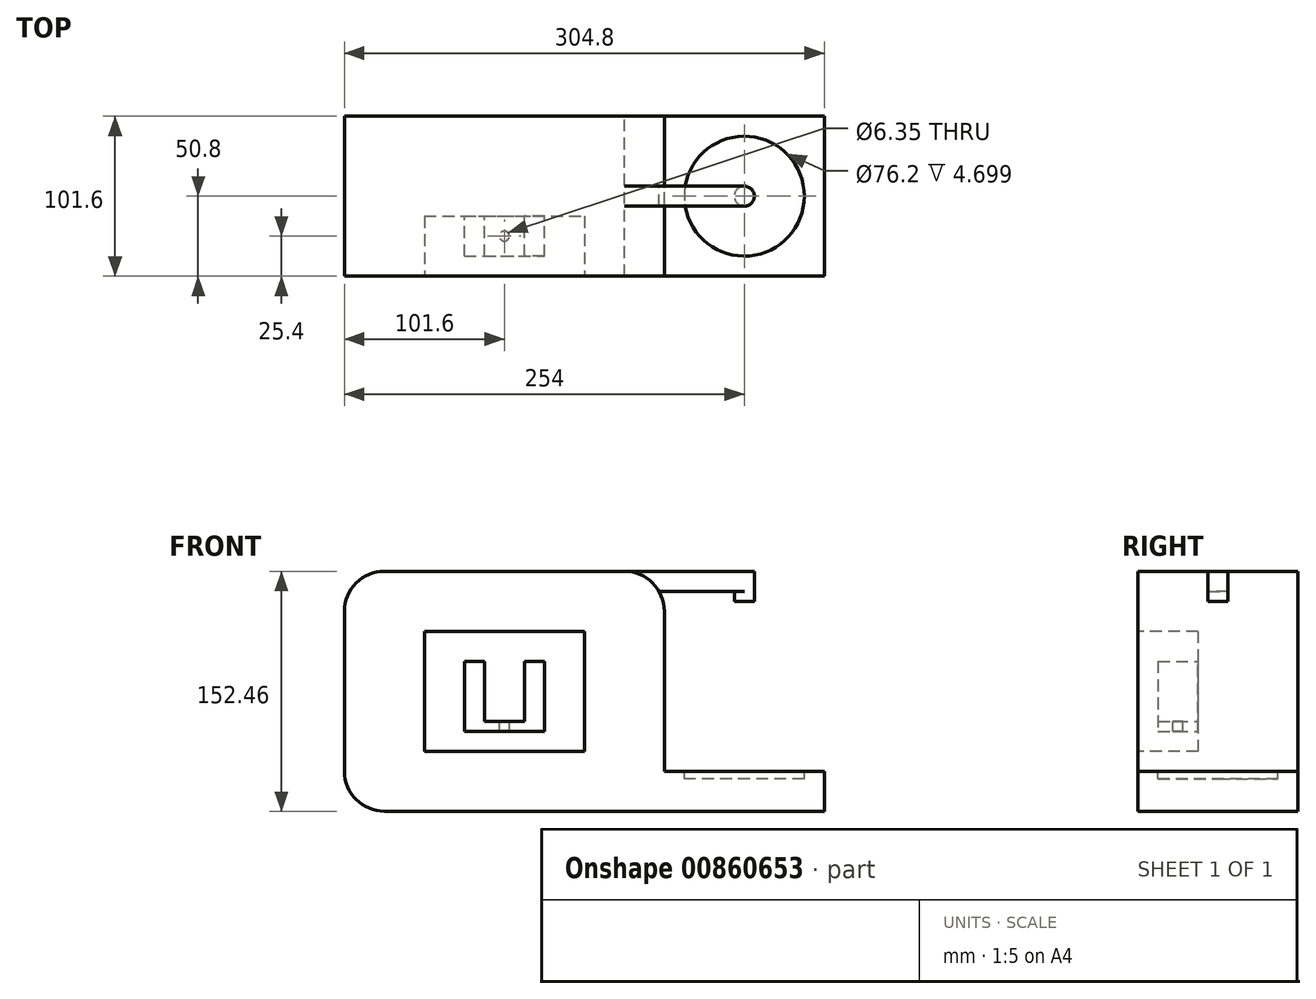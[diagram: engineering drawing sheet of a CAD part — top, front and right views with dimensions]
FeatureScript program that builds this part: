
annotation { "Feature Type Name" : "Feature", "Feature Type Description" : "" }
export const myFeature = defineFeature(function(context is Context, id is Id, definition is map)
    precondition{}
    {
        {
            var Q0;
            Q0=qCreatedBy(makeId("Front.planeOp"),FACE);
            var sketch = newSketch(context, id + "F0", { "sketchPlane" : qUnion([Q0])});
            skLineSegment(sketch, "E0.bottom", {"start": v(-101.6, 76.2) * mm, "end": v(101.6, 76.2) * mm});
            skLineSegment(sketch, "E0.top", {"start": v(-101.6, -76.2) * mm, "end": v(101.6, -76.2) * mm});
            skLineSegment(sketch, "E0.left", {"start": v(-101.6, 76.2) * mm, "end": v(-101.6, -76.2) * mm});
            skLineSegment(sketch, "E0.right", {"start": v(101.6, 76.2) * mm, "end": v(101.6, -76.2) * mm});
            skSolve(sketch);
        }
        {
            var Q0;
            Q0 = qSketchRegion(id + "F0", true);
            extrude(context, id + "F1", {"entities" : qUnion([Q0]), "depth" : 101.6 * mm, "offsetDistance" : 25.4 * mm});
        }
        {
            var Q0;
            Q0=makeQuery(id+"F1.opExtrude","SWEPT_EDGE",EDGE,{"disambiguationData":[OSD([sQuery(id+"F0.wireOp",EDGE,"E0.bottom"),sQuery(id+"F0.wireOp",EDGE,"E0.right")])]});
            fillet(context, id + "F2", {"entities" : qUnion([Q0]), "radius" : 25.4 * mm, "tangentPropagation" : true, "allowEdgeOverflow" : false});
        }
        {
            var Q0;
            Q0=makeQuery(id+"F1.opExtrude","SWEPT_EDGE",EDGE,{"disambiguationData":[OSD([sQuery(id+"F0.wireOp",EDGE,"E0.bottom"),sQuery(id+"F0.wireOp",EDGE,"E0.left")])]});
            var Q1;
            Q1=makeQuery(id+"F1.opExtrude","SWEPT_EDGE",EDGE,{"disambiguationData":[OSD([sQuery(id+"F0.wireOp",EDGE,"E0.top"),sQuery(id+"F0.wireOp",EDGE,"E0.right")])]});
            var Q2;
            Q2=makeQuery(id+"F1.opExtrude","SWEPT_EDGE",EDGE,{"disambiguationData":[OSD([sQuery(id+"F0.wireOp",EDGE,"E0.top"),sQuery(id+"F0.wireOp",EDGE,"E0.left")])]});
            fillet(context, id + "F3", {"entities" : qUnion([Q0, Q1, Q2]), "radius" : 25.4 * mm, "tangentPropagation" : true, "allowEdgeOverflow" : false});
        }
        {
            var Q0;
            Q0=makeQuery(id+"F1.opExtrude","CAP_FACE",FACE,{"disambiguationData":[OSD([sQuery(id+"F0.wireOp",EDGE,"E0.bottom"),sQuery(id+"F0.wireOp",EDGE,"E0.top"),sQuery(id+"F0.wireOp",EDGE,"E0.left"),sQuery(id+"F0.wireOp",EDGE,"E0.right")])],"isStart":false});
            var sketch = newSketch(context, id + "F4", { "sketchPlane" : qUnion([Q0])});
            skLineSegment(sketch, "E1.bottom", {"start": v(-50.8, 38.1) * mm, "end": v(50.8, 38.1) * mm});
            skLineSegment(sketch, "E1.top", {"start": v(-50.8, -38.1) * mm, "end": v(50.8, -38.1) * mm});
            skLineSegment(sketch, "E1.left", {"start": v(-50.8, 38.1) * mm, "end": v(-50.8, -38.1) * mm});
            skLineSegment(sketch, "E1.right", {"start": v(50.8, 38.1) * mm, "end": v(50.8, -38.1) * mm});
            skSolve(sketch);
        }
        {
            var Q0;
            Q0 = qSketchRegion(id + "F4", true);
            extrude(context, id + "F5", {"entities" : qUnion([Q0]), "operationType" : NewBodyOperationType.REMOVE, "oppositeDirection" : true, "depth" : 38.1 * mm, "offsetDistance" : 25.4 * mm});
        }
        {
            var Q0;
            Q0=makeQuery(id+"F5.boolean.opBoolean","COPY",FACE,{"derivedFrom":makeQuery(id+"F5.opExtrude","CAP_FACE",FACE,{"disambiguationData":[OSD([sQuery(id+"F4.wireOp",EDGE,"E1.bottom"),sQuery(id+"F4.wireOp",EDGE,"E1.top"),sQuery(id+"F4.wireOp",EDGE,"E1.left"),sQuery(id+"F4.wireOp",EDGE,"E1.right")])],"isStart":false})});
            var sketch = newSketch(context, id + "F6", { "sketchPlane" : qUnion([Q0])});
            skLineSegment(sketch, "E2.bottom", {"start": v(-25.4, 19.05) * mm, "end": v(-12.7, 19.05) * mm});
            skLineSegment(sketch, "E2.left", {"start": v(-25.4, 19.05) * mm, "end": v(-25.4, -19.05) * mm});
            skLineSegment(sketch, "E2.right", {"start": v(-12.7, 19.05) * mm, "end": v(-12.7, -19.05) * mm});
            skLineSegment(sketch, "E3.bottom", {"start": v(-12.7, -19.05) * mm, "end": v(12.7, -19.05) * mm});
            skLineSegment(sketch, "E3.top", {"start": v(-25.4, -25.4) * mm, "end": v(25.4, -25.4) * mm});
            skLineSegment(sketch, "E3.right", {"start": v(25.4, -25.4) * mm, "end": v(25.4, -19.05) * mm});
            skLineSegment(sketch, "E4", {"start": v(-25.4, -25.4) * mm, "end": v(-25.4, -19.05) * mm});
            skLineSegment(sketch, "E5.MirrorCS", {"start": v(12.7, 19.05) * mm, "end": v(12.7, -19.05) * mm});
            skLineSegment(sketch, "E6.MirrorCS", {"start": v(25.4, 19.05) * mm, "end": v(12.7, 19.05) * mm});
            skLineSegment(sketch, "E7.MirrorCS", {"start": v(25.4, 19.05) * mm, "end": v(25.4, -19.05) * mm});
            skSolve(sketch);
        }
        {
            var Q0;
            Q0 = qSketchRegion(id + "F6", true);
            extrude(context, id + "F7", {"entities" : qUnion([Q0]), "operationType" : NewBodyOperationType.ADD, "depth" : 25.4 * mm, "offsetDistance" : 25.4 * mm});
        }
        {
            var Q0;
            Q0=makeQuery(id+"F7.opExtrude","SWEPT_FACE",FACE,{"disambiguationData":[OSD([sQuery(id+"F6.wireOp",EDGE,"E3.bottom")])]});
            var sketch = newSketch(context, id + "F8", { "sketchPlane" : qUnion([Q0])});
            skCircle(sketch, "E8", {"center": v(0, -76.2) * mm, "radius": 3.18 * mm});
            skSolve(sketch);
        }
        {
            var Q0;
            Q0 = qSketchRegion(id + "F8", true);
            extrude(context, id + "F9", {"entities" : qUnion([Q0]), "operationType" : NewBodyOperationType.REMOVE, "oppositeDirection" : true, "depth" : 12.7 * mm, "offsetDistance" : 25.4 * mm});
        }
        {
            var Q0;
            Q0=makeQuery(id+"F1.opExtrude","SWEPT_FACE",FACE,{"disambiguationData":[OSD([sQuery(id+"F0.wireOp",EDGE,"E0.right")])]});
            var sketch = newSketch(context, id + "F10", { "sketchPlane" : qUnion([Q0])});
            skLineSegment(sketch, "E9.bottom", {"start": v(-101.6, -50.8) * mm, "end": v(0, -50.8) * mm});
            skLineSegment(sketch, "E9.top", {"start": v(-101.6, -76.26) * mm, "end": v(0, -76.26) * mm});
            skLineSegment(sketch, "E9.left", {"start": v(-101.6, -50.8) * mm, "end": v(-101.6, -76.26) * mm});
            skLineSegment(sketch, "E9.right", {"start": v(0, -50.8) * mm, "end": v(0, -76.26) * mm});
            skSolve(sketch);
        }
        {
            var Q0;
            Q0=makeQuery(id+"F10.imprint","IMPRINT",FACE,{"disambiguationData":[TD([[makeQuery(id+"F10.imprint","IMPRINT",EDGE,{"derivedFrom":sQuery(id+"F10.wireOp",EDGE,"E9.bottom")}),-1.0]])]});
            extrude(context, id + "F11", {"entities" : qUnion([Q0]), "operationType" : NewBodyOperationType.ADD, "depth" : 101.6 * mm, "offsetDistance" : 25.4 * mm, "hasSecondDirection" : true, "secondDirectionOppositeDirection" : true, "secondDirectionDepth" : 25.4 * mm});
        }
        {
            var Q0;
            Q0=makeQuery(id+"F11.opExtrude","SWEPT_FACE",FACE,{"disambiguationData":[OSD([sQuery(id+"F10.wireOp",EDGE,"E9.bottom")])]});
            var sketch = newSketch(context, id + "F12", { "sketchPlane" : qUnion([Q0])});
            skCircle(sketch, "E10", {"center": v(152.4, -50.8) * mm, "radius": 38.1 * mm});
            skSolve(sketch);
        }
        {
            var Q0;
            Q0 = qSketchRegion(id + "F12", true);
            extrude(context, id + "F13", {"entities" : qUnion([Q0]), "operationType" : NewBodyOperationType.REMOVE, "oppositeDirection" : true, "depth" : 4.7 * mm, "offsetDistance" : 25.4 * mm});
        }
        {
            var Q0;
            Q0=makeQuery(id+"F11.boolean.opBoolean","MERGE",FACE,{"derivedFrom":[makeQuery(id+"F1.opExtrude","CAP_FACE",FACE,{"disambiguationData":[OSD([sQuery(id+"F0.wireOp",EDGE,"E0.bottom"),sQuery(id+"F0.wireOp",EDGE,"E0.top"),sQuery(id+"F0.wireOp",EDGE,"E0.left"),sQuery(id+"F0.wireOp",EDGE,"E0.right")])],"isStart":true}),makeQuery(id+"F11.opExtrude","SWEPT_FACE",FACE,{"disambiguationData":[OSD([sQuery(id+"F10.wireOp",EDGE,"E9.right")])]})]});
            cPlane(context, id + "F14", {"entities" : qUnion([Q0]), "cplaneType" : CPlaneType.OFFSET, "offset" : 50.8 * mm, "oppositeDirection" : true, "width" : 152.4 * mm, "height" : 152.4 * mm});
        }
        {
            var Q0;
            Q0=qCreatedBy(id+"F14.planeOp",FACE);
            var sketch = newSketch(context, id + "F15", { "sketchPlane" : qUnion([Q0])});
            skLineSegment(sketch, "E11.bottom", {"start": v(-152.4, 76.2) * mm, "end": v(0, 76.2) * mm});
            skLineSegment(sketch, "E11.top", {"start": v(-152.4, 63.5) * mm, "end": v(0, 63.5) * mm});
            skLineSegment(sketch, "E11.left", {"start": v(-152.4, 76.2) * mm, "end": v(-152.4, 63.5) * mm});
            skLineSegment(sketch, "E11.right", {"start": v(0, 76.2) * mm, "end": v(0, 63.5) * mm});
            skSolve(sketch);
        }
        {
            var Q0;
            Q0 = qSketchRegion(id + "F15", true);
            extrude(context, id + "F16", {"entities" : qUnion([Q0]), "operationType" : NewBodyOperationType.ADD, "depth" : 6.35 * mm, "offsetDistance" : 25.4 * mm, "hasSecondDirection" : true, "secondDirectionOppositeDirection" : true, "secondDirectionDepth" : 6.35 * mm});
        }
        {
            var Q0;
            Q0=makeQuery(id+"F16.boolean.opBoolean","MERGE",FACE,{"derivedFrom":[makeQuery(id+"F1.opExtrude","SWEPT_FACE",FACE,{"disambiguationData":[OSD([sQuery(id+"F0.wireOp",EDGE,"E0.bottom")])]}),makeQuery(id+"F16.opExtrude","SWEPT_FACE",FACE,{"disambiguationData":[OSD([sQuery(id+"F15.wireOp",EDGE,"E11.bottom")])]})]});
            var sketch = newSketch(context, id + "F17", { "sketchPlane" : qUnion([Q0])});
            skCircle(sketch, "E12", {"center": v(152.4, -50.8) * mm, "radius": 6.35 * mm});
            skPoint(sketch, "E12.centerSnap0", {"position": v(152.4, -50.8) * mm});
            skSolve(sketch);
        }
        {
            var Q0;
            Q0 = qSketchRegion(id + "F17", true);
            extrude(context, id + "F18", {"entities" : qUnion([Q0]), "operationType" : NewBodyOperationType.ADD, "oppositeDirection" : true, "depth" : 19.05 * mm, "offsetDistance" : 25.4 * mm});
        }
    });
